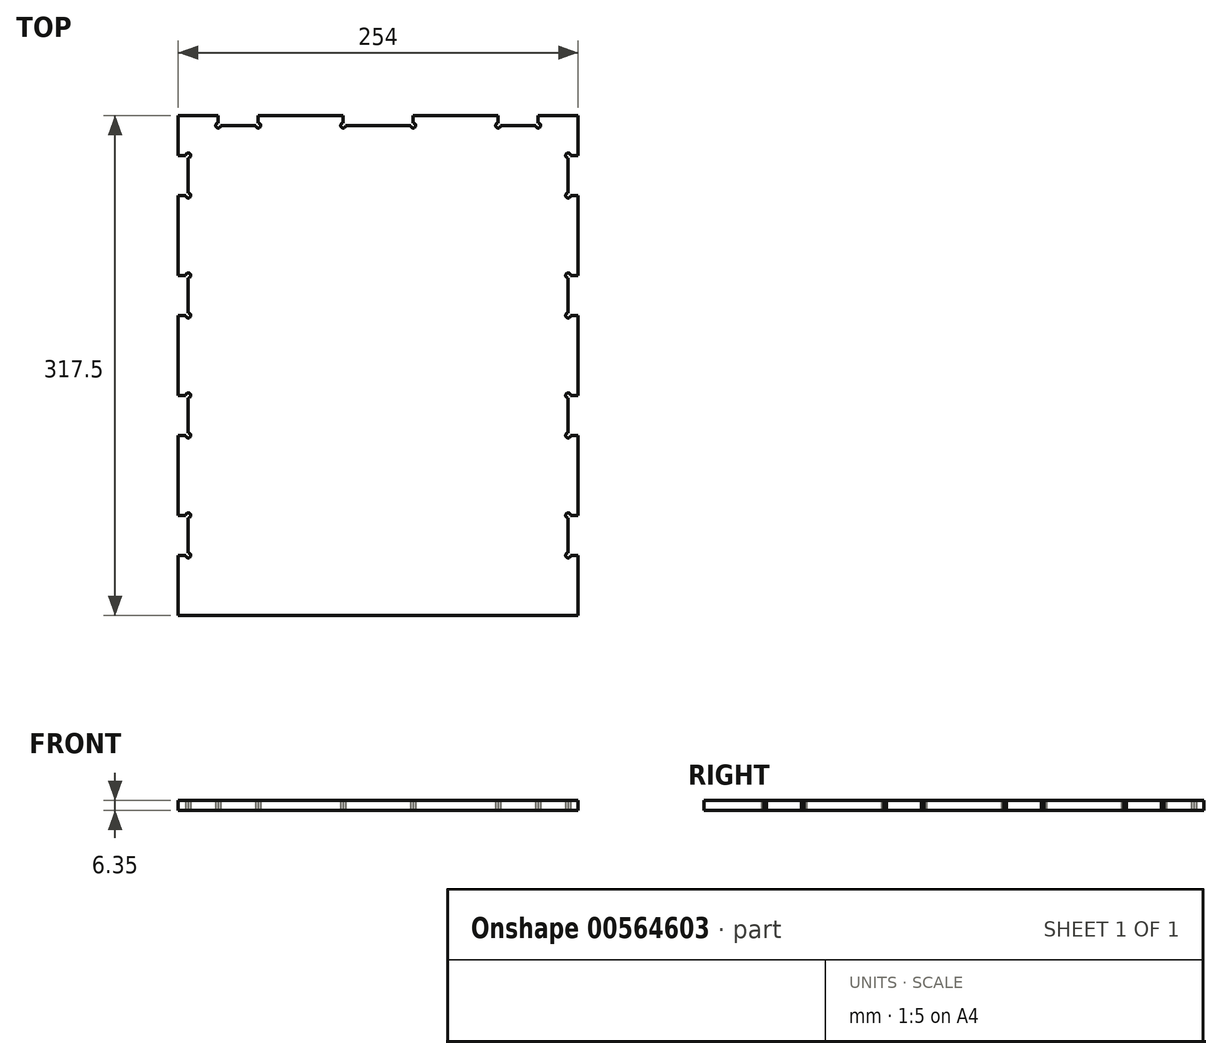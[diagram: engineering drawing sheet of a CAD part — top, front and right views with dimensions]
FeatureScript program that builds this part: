
annotation { "Feature Type Name" : "Feature", "Feature Type Description" : "" }
export const myFeature = defineFeature(function(context is Context, id is Id, definition is map)
    precondition{}
    {
        {
            var Q0;
            Q0=qCreatedBy(makeId("Top.planeOp"),FACE);
            var sketch = newSketch(context, id + "F0", { "sketchPlane" : qUnion([Q0])});
            skLineSegment(sketch, "E0.bottom", {"start": v(-128.99, 203.2) * mm, "end": v(125.01, 203.2) * mm});
            skLineSegment(sketch, "E0.top", {"start": v(-128.99, -114.3) * mm, "end": v(125.01, -114.3) * mm});
            skLineSegment(sketch, "E0.left", {"start": v(-128.99, 203.2) * mm, "end": v(-128.99, -114.3) * mm});
            skLineSegment(sketch, "E0.right", {"start": v(125.01, 203.2) * mm, "end": v(125.01, -114.3) * mm});
            skLineSegment(sketch, "E1.bottom", {"start": v(-103.59, 203.2) * mm, "end": v(-78.19, 203.2) * mm});
            skLineSegment(sketch, "E1.top", {"start": v(-103.59, 196.85) * mm, "end": v(-78.19, 196.85) * mm});
            skLineSegment(sketch, "E1.left", {"start": v(-103.59, 203.2) * mm, "end": v(-103.59, 196.85) * mm});
            skLineSegment(sketch, "E1.right", {"start": v(-78.19, 203.2) * mm, "end": v(-78.19, 196.85) * mm});
            skLineSegment(sketch, "E2.bottom", {"start": v(-24.21, 203.2) * mm, "end": v(20.24, 203.2) * mm});
            skLineSegment(sketch, "E2.top", {"start": v(-24.21, 196.85) * mm, "end": v(20.24, 196.85) * mm});
            skLineSegment(sketch, "E2.left", {"start": v(-24.21, 203.2) * mm, "end": v(-24.21, 196.85) * mm});
            skLineSegment(sketch, "E2.right", {"start": v(20.24, 203.2) * mm, "end": v(20.24, 196.85) * mm});
            skLineSegment(sketch, "E3.bottom", {"start": v(-128.99, 177.8) * mm, "end": v(-122.64, 177.8) * mm});
            skLineSegment(sketch, "E3.top", {"start": v(-128.99, 152.4) * mm, "end": v(-122.64, 152.4) * mm});
            skLineSegment(sketch, "E3.left", {"start": v(-128.99, 177.8) * mm, "end": v(-128.99, 152.4) * mm});
            skLineSegment(sketch, "E3.right", {"start": v(-122.64, 177.8) * mm, "end": v(-122.64, 152.4) * mm});
            skLineSegment(sketch, "E4.bottom", {"start": v(-128.99, 101.6) * mm, "end": v(-122.64, 101.6) * mm});
            skLineSegment(sketch, "E4.top", {"start": v(-128.99, 76.2) * mm, "end": v(-122.64, 76.2) * mm});
            skLineSegment(sketch, "E4.left", {"start": v(-128.99, 101.6) * mm, "end": v(-128.99, 76.2) * mm});
            skLineSegment(sketch, "E4.right", {"start": v(-122.64, 101.6) * mm, "end": v(-122.64, 76.2) * mm});
            skLineSegment(sketch, "E5.bottom", {"start": v(-128.99, -50.8) * mm, "end": v(-122.64, -50.8) * mm});
            skLineSegment(sketch, "E5.top", {"start": v(-128.99, -76.2) * mm, "end": v(-122.64, -76.2) * mm});
            skLineSegment(sketch, "E5.left", {"start": v(-128.99, -50.8) * mm, "end": v(-128.99, -76.2) * mm});
            skLineSegment(sketch, "E5.right", {"start": v(-122.64, -50.8) * mm, "end": v(-122.64, -76.2) * mm});
            skLineSegment(sketch, "E6.bottom", {"start": v(125.01, 177.8) * mm, "end": v(118.66, 177.8) * mm});
            skLineSegment(sketch, "E6.top", {"start": v(125.01, 152.4) * mm, "end": v(118.66, 152.4) * mm});
            skLineSegment(sketch, "E6.left", {"start": v(125.01, 177.8) * mm, "end": v(125.01, 152.4) * mm});
            skLineSegment(sketch, "E6.right", {"start": v(118.66, 177.8) * mm, "end": v(118.66, 152.4) * mm});
            skLineSegment(sketch, "E7.bottom", {"start": v(125.01, 101.6) * mm, "end": v(118.66, 101.6) * mm});
            skLineSegment(sketch, "E7.top", {"start": v(125.01, 76.2) * mm, "end": v(118.66, 76.2) * mm});
            skLineSegment(sketch, "E7.left", {"start": v(125.01, 101.6) * mm, "end": v(125.01, 76.2) * mm});
            skLineSegment(sketch, "E7.right", {"start": v(118.66, 101.6) * mm, "end": v(118.66, 76.2) * mm});
            skLineSegment(sketch, "E8.bottom", {"start": v(125.01, -50.8) * mm, "end": v(118.66, -50.8) * mm});
            skLineSegment(sketch, "E8.top", {"start": v(125.01, -76.2) * mm, "end": v(118.66, -76.2) * mm});
            skLineSegment(sketch, "E8.left", {"start": v(125.01, -50.8) * mm, "end": v(125.01, -76.2) * mm});
            skLineSegment(sketch, "E8.right", {"start": v(118.66, -50.8) * mm, "end": v(118.66, -76.2) * mm});
            skLineSegment(sketch, "E9.bottom", {"start": v(74.21, 203.2) * mm, "end": v(99.61, 203.2) * mm});
            skLineSegment(sketch, "E9.top", {"start": v(74.21, 196.85) * mm, "end": v(99.61, 196.85) * mm});
            skLineSegment(sketch, "E9.left", {"start": v(74.21, 203.2) * mm, "end": v(74.21, 196.85) * mm});
            skLineSegment(sketch, "E9.right", {"start": v(99.61, 203.2) * mm, "end": v(99.61, 196.85) * mm});
            skPoint(sketch, "E10.oppositeSnap0", {"position": v(118.66, 88.9) * mm});
            skLineSegment(sketch, "E10.bottom", {"start": v(125.01, 25.4) * mm, "end": v(118.66, 25.4) * mm});
            skLineSegment(sketch, "E10.top", {"start": v(125.01, 0) * mm, "end": v(118.66, 0) * mm});
            skLineSegment(sketch, "E10.left", {"start": v(125.01, 25.4) * mm, "end": v(125.01, 0) * mm});
            skLineSegment(sketch, "E10.right", {"start": v(118.66, 25.4) * mm, "end": v(118.66, 0) * mm});
            skLineSegment(sketch, "E11.bottom", {"start": v(-128.99, 25.4) * mm, "end": v(-122.64, 25.4) * mm});
            skLineSegment(sketch, "E11.top", {"start": v(-128.99, 0) * mm, "end": v(-122.64, 0) * mm});
            skLineSegment(sketch, "E11.left", {"start": v(-128.99, 25.4) * mm, "end": v(-128.99, 0) * mm});
            skLineSegment(sketch, "E11.right", {"start": v(-122.64, 25.4) * mm, "end": v(-122.64, 0) * mm});
            skCircle(sketch, "E12", {"center": v(-122.64, 177.8) * mm, "radius": 1.59 * mm});
            skCircle(sketch, "E13", {"center": v(-122.64, 152.4) * mm, "radius": 1.59 * mm});
            skCircle(sketch, "E14", {"center": v(-103.59, 196.85) * mm, "radius": 1.59 * mm});
            skCircle(sketch, "E15", {"center": v(-78.19, 196.85) * mm, "radius": 1.59 * mm});
            skCircle(sketch, "E16", {"center": v(-122.64, 101.6) * mm, "radius": 1.59 * mm});
            skCircle(sketch, "E17", {"center": v(-24.21, 196.85) * mm, "radius": 1.59 * mm});
            skCircle(sketch, "E18", {"center": v(20.24, 196.85) * mm, "radius": 1.59 * mm});
            skCircle(sketch, "E19", {"center": v(74.21, 196.85) * mm, "radius": 1.59 * mm});
            skCircle(sketch, "E20", {"center": v(99.61, 196.85) * mm, "radius": 1.59 * mm});
            skCircle(sketch, "E21", {"center": v(118.66, 177.8) * mm, "radius": 1.59 * mm});
            skCircle(sketch, "E22", {"center": v(118.66, 152.4) * mm, "radius": 1.59 * mm});
            skCircle(sketch, "E23", {"center": v(118.66, 101.6) * mm, "radius": 1.59 * mm});
            skCircle(sketch, "E24", {"center": v(118.66, 76.2) * mm, "radius": 1.59 * mm});
            skCircle(sketch, "E25", {"center": v(118.66, 25.4) * mm, "radius": 1.59 * mm});
            skCircle(sketch, "E26", {"center": v(-122.64, 76.2) * mm, "radius": 1.59 * mm});
            skCircle(sketch, "E27", {"center": v(-122.64, 25.4) * mm, "radius": 1.59 * mm});
            skCircle(sketch, "E28", {"center": v(118.66, 0) * mm, "radius": 1.59 * mm});
            skCircle(sketch, "E29", {"center": v(-122.64, 0) * mm, "radius": 1.59 * mm});
            skCircle(sketch, "E30", {"center": v(-122.64, -50.8) * mm, "radius": 1.59 * mm});
            skCircle(sketch, "E31", {"center": v(118.66, -50.8) * mm, "radius": 1.59 * mm});
            skCircle(sketch, "E32", {"center": v(118.66, -76.2) * mm, "radius": 1.59 * mm});
            skCircle(sketch, "E33", {"center": v(-122.64, -76.2) * mm, "radius": 1.59 * mm});
            skSolve(sketch);
        }
        {
            var Q0;
            {var subQ81=sQuery(id+"F0.wireOp",EDGE,"E0.top");Q0=makeQuery(id+"F0.imprint","IMPRINT",FACE,{"disambiguationData":[TD([[makeQuery(id+"F0.imprint","IMPRINT",EDGE,{"derivedFrom":subQ81}),1.0]])]});}
            extrude(context, id + "F1", {"entities" : qUnion([Q0]), "depth" : 6.35 * mm, "offsetDistance" : 25.4 * mm});
        }
    });
